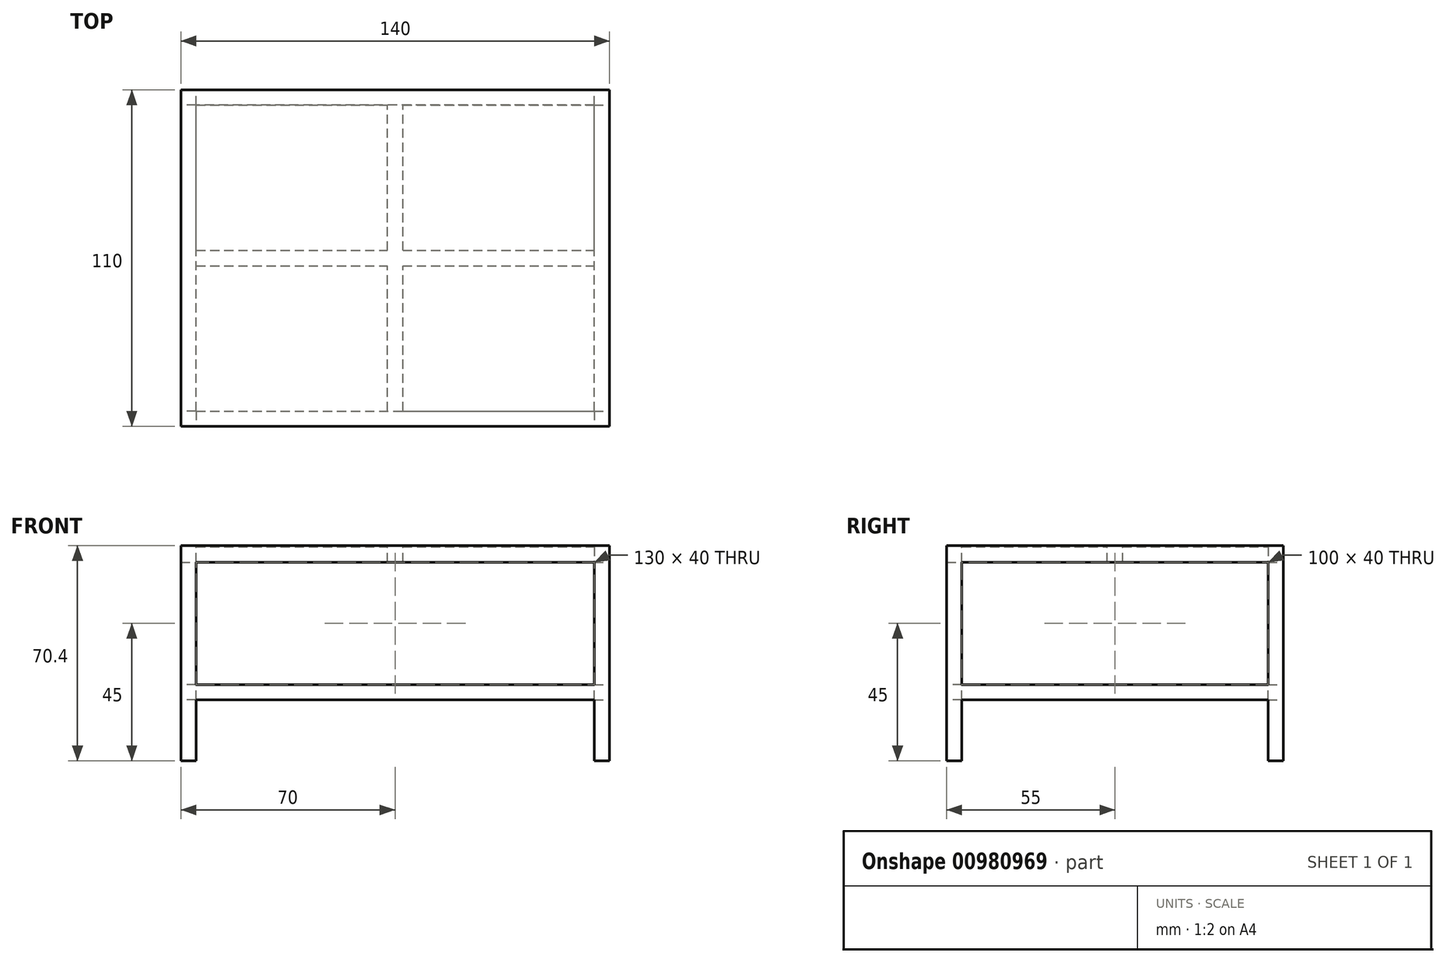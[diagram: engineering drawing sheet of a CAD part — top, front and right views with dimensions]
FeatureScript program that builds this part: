
annotation { "Feature Type Name" : "Feature", "Feature Type Description" : "" }
export const myFeature = defineFeature(function(context is Context, id is Id, definition is map)
    precondition{}
    {
        {
            var Q0;
            Q0=qCreatedBy(makeId("Top.planeOp"),FACE);
            var sketch = newSketch(context, id + "F0", { "sketchPlane" : qUnion([Q0])});
            skLineSegment(sketch, "E0.bottom", {"start": v(-70, 55) * mm, "end": v(70, 55) * mm});
            skLineSegment(sketch, "E0.top", {"start": v(-70, -55) * mm, "end": v(70, -55) * mm});
            skLineSegment(sketch, "E0.left", {"start": v(-70, 55) * mm, "end": v(-70, -55) * mm});
            skLineSegment(sketch, "E0.right", {"start": v(70, 55) * mm, "end": v(70, -55) * mm});
            skSolve(sketch);
        }
        {
            var Q0;
            Q0 = qSketchRegion(id + "F0", true);
            extrude(context, id + "F1", {"entities" : qUnion([Q0]), "depth" : 0.4 * mm, "offsetDistance" : 25 * mm});
        }
        {
            var Q0;
            Q0=makeQuery(id+"F1.opExtrude","CAP_FACE",FACE,{"disambiguationData":[OSD([sQuery(id+"F0.wireOp",EDGE,"E0.bottom"),sQuery(id+"F0.wireOp",EDGE,"E0.top"),sQuery(id+"F0.wireOp",EDGE,"E0.left"),sQuery(id+"F0.wireOp",EDGE,"E0.right")])],"isStart":true});
            var sketch = newSketch(context, id + "F2", { "sketchPlane" : qUnion([Q0])});
            skLineSegment(sketch, "E1.bottom", {"start": v(-70, 55) * mm, "end": v(-65, 55) * mm});
            skLineSegment(sketch, "E1.top", {"start": v(-70, 50) * mm, "end": v(-65, 50) * mm});
            skLineSegment(sketch, "E1.left", {"start": v(-70, 55) * mm, "end": v(-70, 50) * mm});
            skLineSegment(sketch, "E1.right", {"start": v(-65, 55) * mm, "end": v(-65, 50) * mm});
            skLineSegment(sketch, "E2.0.1.0", {"start": v(-65, -50) * mm, "end": v(-65, -55) * mm});
            skLineSegment(sketch, "E2.0.1.1", {"start": v(-70, -55) * mm, "end": v(-65, -55) * mm});
            skLineSegment(sketch, "E2.0.1.2", {"start": v(-70, -50) * mm, "end": v(-70, -55) * mm});
            skLineSegment(sketch, "E2.0.1.3", {"start": v(-70, -50) * mm, "end": v(-65, -50) * mm});
            skLineSegment(sketch, "E2.1.0.0", {"start": v(70, 55) * mm, "end": v(70, 50) * mm});
            skLineSegment(sketch, "E2.1.0.1", {"start": v(65, 50) * mm, "end": v(70, 50) * mm});
            skLineSegment(sketch, "E2.1.0.2", {"start": v(65, 55) * mm, "end": v(65, 50) * mm});
            skLineSegment(sketch, "E2.1.0.3", {"start": v(65, 55) * mm, "end": v(70, 55) * mm});
            skLineSegment(sketch, "E2.1.1.0", {"start": v(70, -50) * mm, "end": v(70, -55) * mm});
            skLineSegment(sketch, "E2.1.1.1", {"start": v(65, -55) * mm, "end": v(70, -55) * mm});
            skLineSegment(sketch, "E2.1.1.2", {"start": v(65, -50) * mm, "end": v(65, -55) * mm});
            skLineSegment(sketch, "E2.1.1.3", {"start": v(65, -50) * mm, "end": v(70, -50) * mm});
            skLineSegment(sketch, "E2.direction1", {"start": v(-65, 50) * mm, "end": v(70, 50) * mm, "construction": true});
            skLineSegment(sketch, "E2.direction2", {"start": v(-65, 50) * mm, "end": v(-65, -55) * mm, "construction": true});
            skSolve(sketch);
        }
        {
            var Q0;
            Q0 = qSketchRegion(id + "F2", true);
            extrude(context, id + "F3", {"entities" : qUnion([Q0]), "operationType" : NewBodyOperationType.ADD, "depth" : 70 * mm, "offsetDistance" : 25 * mm});
        }
        {
            var Q0;
            Q0=makeQuery(id+"F1.opExtrude","CAP_FACE",FACE,{"disambiguationData":[OSD([sQuery(id+"F0.wireOp",EDGE,"E0.bottom"),sQuery(id+"F0.wireOp",EDGE,"E0.top"),sQuery(id+"F0.wireOp",EDGE,"E0.left"),sQuery(id+"F0.wireOp",EDGE,"E0.right")])],"isStart":true});
            var sketch = newSketch(context, id + "F4", { "sketchPlane" : qUnion([Q0])});
            skLineSegment(sketch, "E3.bottom", {"start": v(-65, 55) * mm, "end": v(65, 55) * mm});
            skLineSegment(sketch, "E3.top", {"start": v(-65, 50) * mm, "end": v(65, 50) * mm});
            skLineSegment(sketch, "E3.left", {"start": v(-65, 55) * mm, "end": v(-65, 50) * mm});
            skLineSegment(sketch, "E3.right", {"start": v(65, 55) * mm, "end": v(65, 50) * mm});
            skLineSegment(sketch, "E4.bottom", {"start": v(-65, 50) * mm, "end": v(-70, 50) * mm});
            skLineSegment(sketch, "E4.top", {"start": v(-65, -50) * mm, "end": v(-70, -50) * mm});
            skLineSegment(sketch, "E4.left", {"start": v(-65, 50) * mm, "end": v(-65, -50) * mm});
            skLineSegment(sketch, "E4.right", {"start": v(-70, 50) * mm, "end": v(-70, -50) * mm});
            skLineSegment(sketch, "E5.bottom", {"start": v(-65, -50) * mm, "end": v(65, -50) * mm});
            skLineSegment(sketch, "E5.top", {"start": v(-65, -55) * mm, "end": v(65, -55) * mm});
            skLineSegment(sketch, "E5.left", {"start": v(-65, -50) * mm, "end": v(-65, -55) * mm});
            skLineSegment(sketch, "E5.right", {"start": v(65, -50) * mm, "end": v(65, -55) * mm});
            skLineSegment(sketch, "E6.bottom", {"start": v(65, -50) * mm, "end": v(70, -50) * mm});
            skLineSegment(sketch, "E6.top", {"start": v(65, 50) * mm, "end": v(70, 50) * mm});
            skLineSegment(sketch, "E6.left", {"start": v(65, -50) * mm, "end": v(65, 50) * mm});
            skLineSegment(sketch, "E6.right", {"start": v(70, -50) * mm, "end": v(70, 50) * mm});
            skSolve(sketch);
        }
        {
            var Q0;
            Q0 = qSketchRegion(id + "F4", true);
            extrude(context, id + "F5", {"entities" : qUnion([Q0]), "operationType" : NewBodyOperationType.ADD, "depth" : 5 * mm, "offsetDistance" : 25 * mm});
        }
        {
            var Q0;
            Q0=makeQuery(id+"F5.opExtrude","CAP_FACE",FACE,{"disambiguationData":[OSD([sQuery(id+"F4.wireOp",EDGE,"E3.bottom"),sQuery(id+"F4.wireOp",EDGE,"E3.left"),sQuery(id+"F4.wireOp",EDGE,"E3.right"),sQuery(id+"F4.wireOp",EDGE,"E4.bottom"),sQuery(id+"F4.wireOp",EDGE,"E4.top"),sQuery(id+"F4.wireOp",EDGE,"E4.right"),sQuery(id+"F4.wireOp",EDGE,"E5.top"),sQuery(id+"F4.wireOp",EDGE,"E5.left"),sQuery(id+"F4.wireOp",EDGE,"E5.right"),sQuery(id+"F4.wireOp",EDGE,"E6.bottom"),sQuery(id+"F4.wireOp",EDGE,"E6.top"),sQuery(id+"F4.wireOp",EDGE,"E6.right")])],"isStart":false});
            var sketch = newSketch(context, id + "F6", { "sketchPlane" : qUnion([Q0])});
            skLineSegment(sketch, "E7.bottom", {"start": v(-65, 50) * mm, "end": v(65, 50) * mm});
            skLineSegment(sketch, "E7.top", {"start": v(-65, -50) * mm, "end": v(65, -50) * mm});
            skLineSegment(sketch, "E7.left", {"start": v(-65, 50) * mm, "end": v(-65, -50) * mm});
            skLineSegment(sketch, "E7.right", {"start": v(65, 50) * mm, "end": v(65, -50) * mm});
            skSolve(sketch);
        }
        {
            var Q0;
            Q0 = qSketchRegion(id + "F6", true);
            extrude(context, id + "F7", {"entities" : qUnion([Q0]), "operationType" : NewBodyOperationType.REMOVE, "oppositeDirection" : true, "depth" : 5 * mm, "offsetDistance" : 25 * mm});
        }
        {
            var Q0;
            Q0=makeQuery(id+"F7.boolean.opBoolean","COPY",FACE,{"derivedFrom":makeQuery(id+"F7.opExtrude","CAP_FACE",FACE,{"disambiguationData":[OSD([sQuery(id+"F6.wireOp",EDGE,"E7.bottom"),sQuery(id+"F6.wireOp",EDGE,"E7.top"),sQuery(id+"F6.wireOp",EDGE,"E7.left"),sQuery(id+"F6.wireOp",EDGE,"E7.right")])],"isStart":false})});
            var sketch = newSketch(context, id + "F8", { "sketchPlane" : qUnion([Q0])});
            skLineSegment(sketch, "E8.bottom", {"start": v(2.5, 50) * mm, "end": v(-2.5, 50) * mm});
            skLineSegment(sketch, "E8.top", {"start": v(2.5, -50) * mm, "end": v(-2.5, -50) * mm});
            skLineSegment(sketch, "E8.left", {"start": v(2.5, 50) * mm, "end": v(2.5, -50) * mm});
            skLineSegment(sketch, "E8.right", {"start": v(-2.5, 50) * mm, "end": v(-2.5, -50) * mm});
            skLineSegment(sketch, "E9.bottom", {"start": v(-65, -2.5) * mm, "end": v(65, -2.5) * mm});
            skLineSegment(sketch, "E9.top", {"start": v(-65, 2.5) * mm, "end": v(65, 2.5) * mm});
            skLineSegment(sketch, "E9.left", {"start": v(-65, -2.5) * mm, "end": v(-65, 2.5) * mm});
            skLineSegment(sketch, "E9.right", {"start": v(65, -2.5) * mm, "end": v(65, 2.5) * mm});
            skSolve(sketch);
        }
        {
            var Q0;
            Q0 = qSketchRegion(id + "F8", true);
            extrude(context, id + "F9", {"entities" : qUnion([Q0]), "operationType" : NewBodyOperationType.ADD, "depth" : 5 * mm, "offsetDistance" : 25 * mm});
        }
        {
            var Q0;
            Q0=makeQuery(id+"F5.boolean.opBoolean","MERGE",FACE,{"derivedFrom":[makeQuery(id+"F3.boolean.opBoolean","MERGE",FACE,{"derivedFrom":[makeQuery(id+"F1.opExtrude","SWEPT_FACE",FACE,{"disambiguationData":[OSD([sQuery(id+"F0.wireOp",EDGE,"E0.top")])]}),makeQuery(id+"F3.opExtrude","SWEPT_FACE",FACE,{"disambiguationData":[OSD([sQuery(id+"F2.wireOp",EDGE,"E1.bottom")])]}),makeQuery(id+"F3.opExtrude","SWEPT_FACE",FACE,{"disambiguationData":[OSD([sQuery(id+"F2.wireOp",EDGE,"E2.1.0.3")])]})]}),makeQuery(id+"F5.opExtrude","SWEPT_FACE",FACE,{"disambiguationData":[OSD([sQuery(id+"F4.wireOp",EDGE,"E3.bottom")])]})]});
            var sketch = newSketch(context, id + "F10", { "sketchPlane" : qUnion([Q0])});
            skLineSegment(sketch, "E10.bottom", {"start": v(-65, -50) * mm, "end": v(65, -50) * mm});
            skLineSegment(sketch, "E10.top", {"start": v(-65, -45) * mm, "end": v(65, -45) * mm});
            skLineSegment(sketch, "E10.left", {"start": v(-65, -50) * mm, "end": v(-65, -45) * mm});
            skLineSegment(sketch, "E10.right", {"start": v(65, -50) * mm, "end": v(65, -45) * mm});
            skSolve(sketch);
        }
        {
            var Q0;
            Q0 = qSketchRegion(id + "F10", true);
            extrude(context, id + "F11", {"entities" : qUnion([Q0]), "operationType" : NewBodyOperationType.ADD, "oppositeDirection" : true, "depth" : 5 * mm, "offsetDistance" : 25 * mm});
        }
        {
            var Q0;
            Q0=makeQuery(id+"F5.boolean.opBoolean","MERGE",FACE,{"derivedFrom":[makeQuery(id+"F3.boolean.opBoolean","MERGE",FACE,{"derivedFrom":[makeQuery(id+"F1.opExtrude","SWEPT_FACE",FACE,{"disambiguationData":[OSD([sQuery(id+"F0.wireOp",EDGE,"E0.right")])]}),makeQuery(id+"F3.opExtrude","SWEPT_FACE",FACE,{"disambiguationData":[OSD([sQuery(id+"F2.wireOp",EDGE,"E2.1.0.0")])]}),makeQuery(id+"F3.opExtrude","SWEPT_FACE",FACE,{"disambiguationData":[OSD([sQuery(id+"F2.wireOp",EDGE,"E2.1.1.0")])]})]}),makeQuery(id+"F5.opExtrude","SWEPT_FACE",FACE,{"disambiguationData":[OSD([sQuery(id+"F4.wireOp",EDGE,"E6.right")])]})]});
            var sketch = newSketch(context, id + "F12", { "sketchPlane" : qUnion([Q0])});
            skLineSegment(sketch, "E11.bottom", {"start": v(-50, -45) * mm, "end": v(50, -45) * mm});
            skLineSegment(sketch, "E11.top", {"start": v(-50, -50) * mm, "end": v(50, -50) * mm});
            skLineSegment(sketch, "E11.left", {"start": v(-50, -45) * mm, "end": v(-50, -50) * mm});
            skLineSegment(sketch, "E11.right", {"start": v(50, -45) * mm, "end": v(50, -50) * mm});
            skSolve(sketch);
        }
        {
            var Q0;
            Q0 = qSketchRegion(id + "F12", true);
            extrude(context, id + "F13", {"entities" : qUnion([Q0]), "operationType" : NewBodyOperationType.ADD, "oppositeDirection" : true, "depth" : 5 * mm, "offsetDistance" : 25 * mm});
        }
        {
            var Q0;
            Q0=makeQuery(id+"F5.boolean.opBoolean","MERGE",FACE,{"derivedFrom":[makeQuery(id+"F3.boolean.opBoolean","MERGE",FACE,{"derivedFrom":[makeQuery(id+"F1.opExtrude","SWEPT_FACE",FACE,{"disambiguationData":[OSD([sQuery(id+"F0.wireOp",EDGE,"E0.left")])]}),makeQuery(id+"F3.opExtrude","SWEPT_FACE",FACE,{"disambiguationData":[OSD([sQuery(id+"F2.wireOp",EDGE,"E1.left")])]}),makeQuery(id+"F3.opExtrude","SWEPT_FACE",FACE,{"disambiguationData":[OSD([sQuery(id+"F2.wireOp",EDGE,"E2.0.1.2")])]})]}),makeQuery(id+"F5.opExtrude","SWEPT_FACE",FACE,{"disambiguationData":[OSD([sQuery(id+"F4.wireOp",EDGE,"E4.right")])]})]});
            var sketch = newSketch(context, id + "F14", { "sketchPlane" : qUnion([Q0])});
            skLineSegment(sketch, "E12.bottom", {"start": v(50, -50) * mm, "end": v(-50, -50) * mm});
            skLineSegment(sketch, "E12.top", {"start": v(50, -45) * mm, "end": v(-50, -45) * mm});
            skLineSegment(sketch, "E12.left", {"start": v(50, -50) * mm, "end": v(50, -45) * mm});
            skLineSegment(sketch, "E12.right", {"start": v(-50, -50) * mm, "end": v(-50, -45) * mm});
            skSolve(sketch);
        }
        {
            var Q0;
            Q0 = qSketchRegion(id + "F14", true);
            extrude(context, id + "F15", {"entities" : qUnion([Q0]), "operationType" : NewBodyOperationType.ADD, "oppositeDirection" : true, "depth" : 5 * mm, "offsetDistance" : 25 * mm});
        }
        {
            var Q0;
            Q0=makeQuery(id+"F5.boolean.opBoolean","MERGE",FACE,{"derivedFrom":[makeQuery(id+"F3.boolean.opBoolean","MERGE",FACE,{"derivedFrom":[makeQuery(id+"F1.opExtrude","SWEPT_FACE",FACE,{"disambiguationData":[OSD([sQuery(id+"F0.wireOp",EDGE,"E0.bottom")])]}),makeQuery(id+"F3.opExtrude","SWEPT_FACE",FACE,{"disambiguationData":[OSD([sQuery(id+"F2.wireOp",EDGE,"E2.0.1.1")])]}),makeQuery(id+"F3.opExtrude","SWEPT_FACE",FACE,{"disambiguationData":[OSD([sQuery(id+"F2.wireOp",EDGE,"E2.1.1.1")])]})]}),makeQuery(id+"F5.opExtrude","SWEPT_FACE",FACE,{"disambiguationData":[OSD([sQuery(id+"F4.wireOp",EDGE,"E5.top")])]})]});
            var sketch = newSketch(context, id + "F16", { "sketchPlane" : qUnion([Q0])});
            skLineSegment(sketch, "E13.bottom", {"start": v(-65, -50) * mm, "end": v(65, -50) * mm});
            skLineSegment(sketch, "E13.top", {"start": v(-65, -45) * mm, "end": v(65, -45) * mm});
            skLineSegment(sketch, "E13.left", {"start": v(-65, -50) * mm, "end": v(-65, -45) * mm});
            skLineSegment(sketch, "E13.right", {"start": v(65, -50) * mm, "end": v(65, -45) * mm});
            skSolve(sketch);
        }
        {
            var Q0;
            Q0 = qSketchRegion(id + "F16", true);
            extrude(context, id + "F17", {"entities" : qUnion([Q0]), "operationType" : NewBodyOperationType.ADD, "oppositeDirection" : true, "depth" : 5 * mm, "offsetDistance" : 25 * mm});
        }
    });
